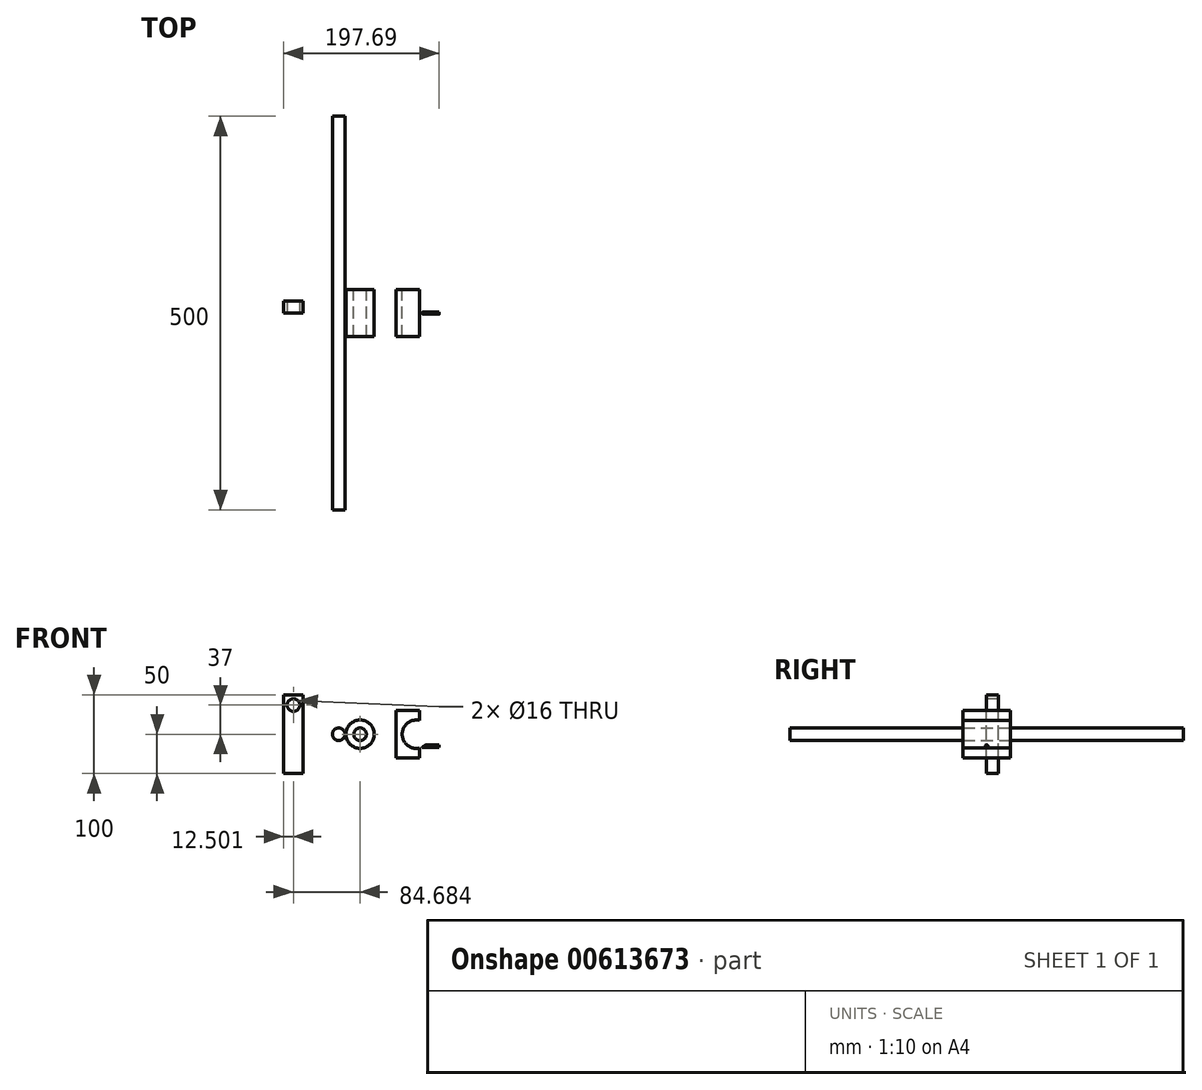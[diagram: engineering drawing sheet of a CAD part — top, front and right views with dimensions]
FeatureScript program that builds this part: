
annotation { "Feature Type Name" : "Feature", "Feature Type Description" : "" }
export const myFeature = defineFeature(function(context is Context, id is Id, definition is map)
    precondition{}
    {
        {
            var Q0;
            Q0=qCreatedBy(makeId("Front.planeOp"),FACE);
            var sketch = newSketch(context, id + "F0", { "sketchPlane" : qUnion([Q0])});
            skCircle(sketch, "E0", {"center": v(-13.97, 0) * mm, "radius": 8 * mm});
            skSolve(sketch);
        }
        {
            var Q0;
            Q0=makeQuery(id+"F0.imprint","IMPRINT",FACE,{"disambiguationData":[TD([[makeQuery(id+"F0.imprint","IMPRINT",EDGE,{"derivedFrom":sQuery(id+"F0.wireOp",EDGE,"E0")}),1.0]])]});
            extrude(context, id + "F1", {"entities" : qUnion([Q0]), "endBound" : BoundingType.SYMMETRIC, "depth" : 500 * mm, "offsetDistance" : 25 * mm});
        }
        {
            var Q0;
            Q0=qCreatedBy(makeId("Front.planeOp"),FACE);
            var sketch = newSketch(context, id + "F2", { "sketchPlane" : qUnion([Q0])});
            skCircle(sketch, "E1", {"center": v(13.14, 0) * mm, "radius": 8 * mm});
            skCircle(sketch, "E2.0", {"center": v(13.14, 0) * mm, "radius": 18 * mm});
            skSolve(sketch);
        }
        {
            var Q0;
            Q0=makeQuery(id+"F2.imprint","IMPRINT",FACE,{"disambiguationData":[TD([[makeQuery(id+"F2.imprint","IMPRINT",EDGE,{"derivedFrom":sQuery(id+"F2.wireOp",EDGE,"E1")}),-1.0]])]});
            extrude(context, id + "F3", {"entities" : qUnion([Q0]), "endBound" : BoundingType.SYMMETRIC, "depth" : 60 * mm, "offsetDistance" : 25 * mm});
        }
        {
            var Q0;
            Q0=qCreatedBy(makeId("Front.planeOp"),FACE);
            var sketch = newSketch(context, id + "F4", { "sketchPlane" : qUnion([Q0])});
            skLineSegment(sketch, "E3.bottom", {"start": v(-59.05, -50) * mm, "end": v(-84.05, -50) * mm});
            skLineSegment(sketch, "E3.top", {"start": v(-59.05, 50) * mm, "end": v(-84.05, 50) * mm});
            skLineSegment(sketch, "E3.left", {"start": v(-59.05, -50) * mm, "end": v(-59.05, 50) * mm});
            skLineSegment(sketch, "E3.right", {"start": v(-84.05, -50) * mm, "end": v(-84.05, 50) * mm});
            skPoint(sketch, "E3.middle", {"position": v(-71.55, 0) * mm});
            skSolve(sketch);
        }
        {
            var Q0;
            Q0=makeQuery(id+"F4.imprint","IMPRINT",FACE,{"disambiguationData":[TD([[makeQuery(id+"F4.imprint","IMPRINT",EDGE,{"derivedFrom":sQuery(id+"F4.wireOp",EDGE,"E3.bottom")}),-1.0]])]});
            extrude(context, id + "F5", {"entities" : qUnion([Q0]), "oppositeDirection" : true, "depth" : 15 * mm, "offsetDistance" : 25 * mm});
        }
        {
            var Q0;
            Q0=makeQuery(id+"F5.opExtrude","CAP_FACE",FACE,{"disambiguationData":[OSD([sQuery(id+"F4.wireOp",EDGE,"E3.bottom"),sQuery(id+"F4.wireOp",EDGE,"E3.top"),sQuery(id+"F4.wireOp",EDGE,"E3.left"),sQuery(id+"F4.wireOp",EDGE,"E3.right")])],"isStart":true});
            var sketch = newSketch(context, id + "F6", { "sketchPlane" : qUnion([Q0])});
            skCircle(sketch, "E4", {"center": v(-71.55, 37) * mm, "radius": 8 * mm});
            skPoint(sketch, "E4.centerSnap0", {"position": v(-71.55, 50) * mm});
            skSolve(sketch);
        }
        {
            var Q0;
            Q0=makeQuery(id+"F6.imprint","IMPRINT",FACE,{"disambiguationData":[TD([[makeQuery(id+"F6.imprint","IMPRINT",EDGE,{"derivedFrom":sQuery(id+"F6.wireOp",EDGE,"E4")}),1.0]])]});
            extrude(context, id + "F7", {"entities" : qUnion([Q0]), "operationType" : NewBodyOperationType.REMOVE, "oppositeDirection" : true, "depth" : 25 * mm, "offsetDistance" : 25 * mm});
        }
        {
            var Q0;
            Q0=qCreatedBy(makeId("Front.planeOp"),FACE);
            var sketch = newSketch(context, id + "F8", { "sketchPlane" : qUnion([Q0])});
            skLineSegment(sketch, "E5.bottom", {"start": v(113.64, -30) * mm, "end": v(58.64, -30) * mm});
            skLineSegment(sketch, "E5.top", {"start": v(113.64, 30) * mm, "end": v(58.64, 30) * mm});
            skLineSegment(sketch, "E5.left", {"start": v(113.64, -30) * mm, "end": v(113.64, 30) * mm});
            skLineSegment(sketch, "E5.right", {"start": v(58.64, -30) * mm, "end": v(58.64, 30) * mm});
            skCircle(sketch, "E6", {"center": v(84.64, 0) * mm, "radius": 18 * mm});
            skSolve(sketch);
        }
        {
            var Q0;
            Q0=makeQuery(id+"F8.imprint","IMPRINT",FACE,{"disambiguationData":[TD([[makeQuery(id+"F8.imprint","IMPRINT",EDGE,{"derivedFrom":sQuery(id+"F8.wireOp",EDGE,"E5.bottom")}),-1.0]])]});
            extrude(context, id + "F9", {"entities" : qUnion([Q0]), "endBound" : BoundingType.SYMMETRIC, "depth" : 60 * mm, "offsetDistance" : 25 * mm});
        }
        {
            var Q0;
            Q0=makeQuery(id+"F9.opExtrude","SWEPT_FACE",FACE,{"disambiguationData":[OSD([sQuery(id+"F8.wireOp",EDGE,"E5.left")])]});
            var sketch = newSketch(context, id + "F10", { "sketchPlane" : qUnion([Q0])});
            skLineSegment(sketch, "E7", {"start": v(0, 30) * mm, "end": v(0, -30) * mm, "construction": true});
            skPoint(sketch, "E8", {"position": v(0, 0) * mm});
            skCircle(sketch, "E9", {"center": v(0, 15) * mm, "radius": 1.5 * mm});
            skCircle(sketch, "E10.MirrorC", {"center": v(0, -15) * mm, "radius": 1.5 * mm});
            skSolve(sketch);
        }
        {
            var Q0;
            Q0=makeQuery(id+"F10.imprint","IMPRINT",FACE,{"disambiguationData":[TD([[makeQuery(id+"F10.imprint","IMPRINT",EDGE,{"derivedFrom":sQuery(id+"F10.wireOp",EDGE,"E9")}),1.0]])]});
            var Q1;
            Q1=makeQuery(id+"F10.imprint","IMPRINT",FACE,{"disambiguationData":[TD([[makeQuery(id+"F10.imprint","IMPRINT",EDGE,{"derivedFrom":sQuery(id+"F10.wireOp",EDGE,"E10.MirrorC")}),-1.0]])]});
            extrude(context, id + "F11", {"entities" : qUnion([Q0, Q1]), "operationType" : NewBodyOperationType.REMOVE, "oppositeDirection" : true, "depth" : 25 * mm, "offsetDistance" : 25 * mm});
        }
    });
